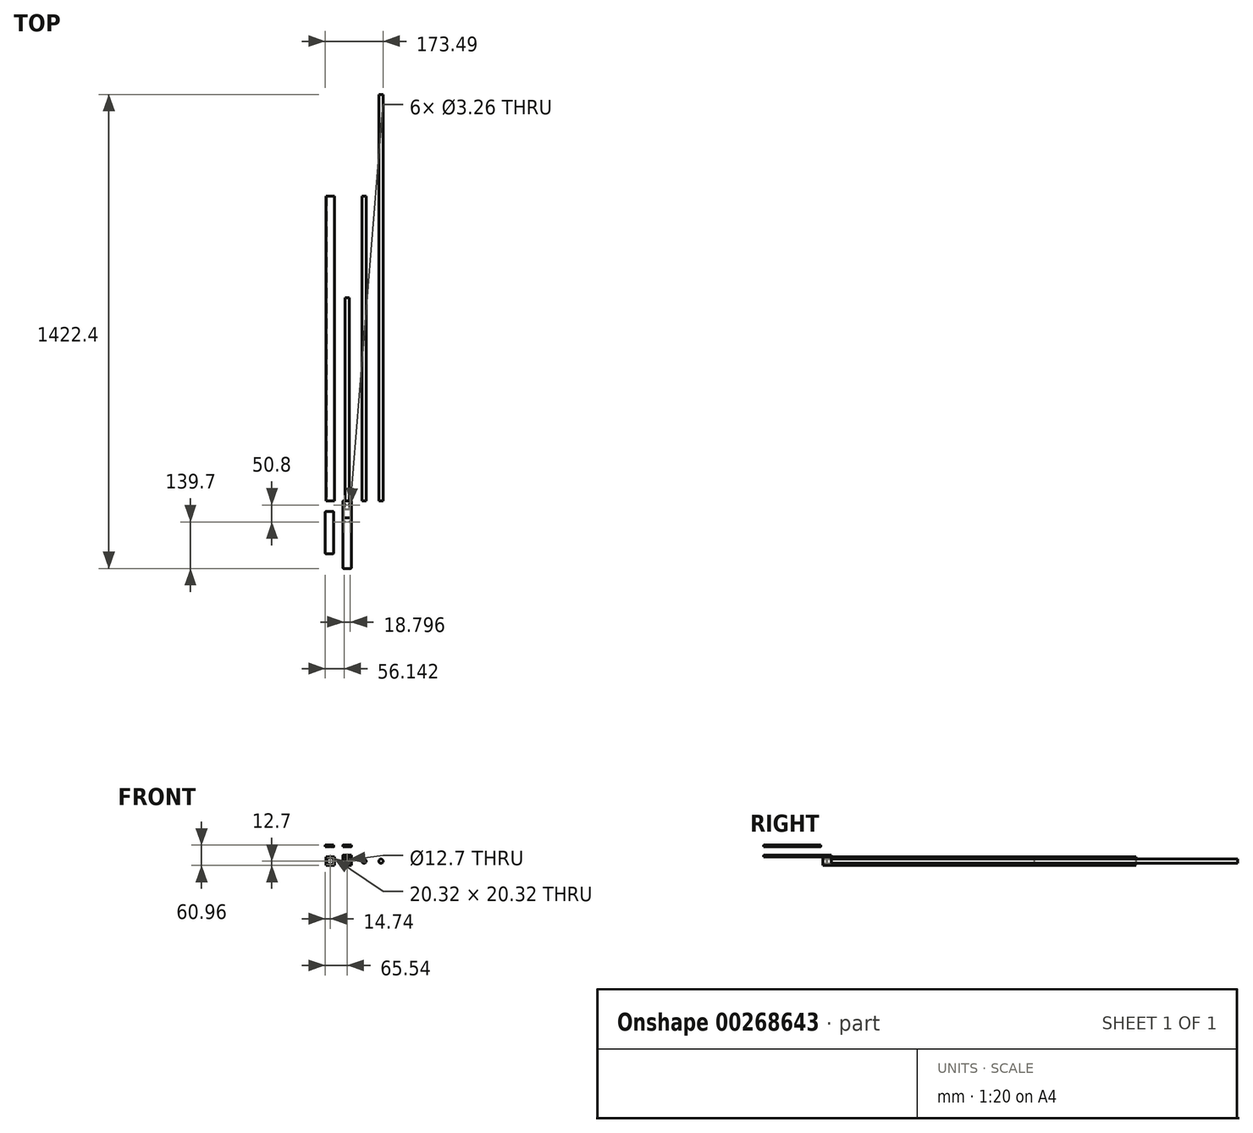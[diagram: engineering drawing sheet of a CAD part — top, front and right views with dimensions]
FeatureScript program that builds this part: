
annotation { "Feature Type Name" : "Feature", "Feature Type Description" : "" }
export const myFeature = defineFeature(function(context is Context, id is Id, definition is map)
    precondition{}
    {
        {
            var Q0;
            Q0=qCreatedBy(makeId("Front.planeOp"),FACE);
            var sketch = newSketch(context, id + "F0", { "sketchPlane" : qUnion([Q0])});
            skCircle(sketch, "E0", {"center": v(0, 0) * mm, "radius": 6.35 * mm});
            skCircle(sketch, "E1", {"center": v(-50.8, 0) * mm, "radius": 6.35 * mm});
            skCircle(sketch, "E2", {"center": v(50.8, 0) * mm, "radius": 6.35 * mm});
            skSolve(sketch);
        }
        {
            var Q0;
            Q0=makeQuery(id+"F0.imprint","IMPRINT",FACE,{"disambiguationData":[TD([[makeQuery(id+"F0.imprint","IMPRINT",EDGE,{"derivedFrom":sQuery(id+"F0.wireOp",EDGE,"E1")}),1.0]])]});
            extrude(context, id + "F1", {"entities" : qUnion([Q0]), "oppositeDirection" : true, "depth" : 609.6 * mm});
        }
        {
            var Q0;
            Q0=makeQuery(id+"F0.imprint","IMPRINT",FACE,{"disambiguationData":[TD([[makeQuery(id+"F0.imprint","IMPRINT",EDGE,{"derivedFrom":sQuery(id+"F0.wireOp",EDGE,"E0")}),1.0]])]});
            var Q1;
            Q1=sQuery(id+"F0.wireOp",EDGE,"E0");
            extrude(context, id + "F2", {"entities" : qUnion([Q0]), "surfaceEntities" : qUnion([Q1]), "oppositeDirection" : true, "depth" : 914.4 * mm});
        }
        {
            var Q0;
            Q0=makeQuery(id+"F0.imprint","IMPRINT",FACE,{"disambiguationData":[TD([[makeQuery(id+"F0.imprint","IMPRINT",EDGE,{"derivedFrom":sQuery(id+"F0.wireOp",EDGE,"E2")}),1.0]])]});
            extrude(context, id + "F3", {"entities" : qUnion([Q0]), "oppositeDirection" : true, "depth" : 1219.2 * mm});
        }
        {
            var Q0;
            Q0=makeQuery(id+"F0.imprint","IMPRINT",FACE,{"disambiguationData":[TD([[makeQuery(id+"F0.imprint","IMPRINT",EDGE,{"derivedFrom":sQuery(id+"F0.wireOp",EDGE,"E1")}),1.0]])]});
            var sketch = newSketch(context, id + "F4", { "sketchPlane" : qUnion([Q0])});
            skCircle(sketch, "E3.0", {"center": v(-50.8, 0) * mm, "radius": 6.35 * mm});
            skLineSegment(sketch, "E4.bottom", {"start": v(-63.5, 12.7) * mm, "end": v(-38.1, 12.7) * mm});
            skLineSegment(sketch, "E4.top", {"start": v(-63.5, -12.7) * mm, "end": v(-38.1, -12.7) * mm});
            skLineSegment(sketch, "E4.left", {"start": v(-63.5, 12.7) * mm, "end": v(-63.5, -12.7) * mm});
            skLineSegment(sketch, "E4.right", {"start": v(-38.1, 12.7) * mm, "end": v(-38.1, -12.7) * mm});
            skSolve(sketch);
        }
        {
            var Q0;
            Q0=makeQuery(id+"F4.imprint","IMPRINT",FACE,{"disambiguationData":[TD([[makeQuery(id+"F4.imprint","IMPRINT",EDGE,{"derivedFrom":sQuery(id+"F4.wireOp",EDGE,"E3.0")}),-1.0]])]});
            extrude(context, id + "F5", {"entities" : qUnion([Q0]), "depth" : 25.4 * mm});
        }
        {
            var Q0;
            Q0=makeQuery(id+"F5.opExtrude","SWEPT_FACE",FACE,{"disambiguationData":[OSD([sQuery(id+"F4.wireOp",EDGE,"E4.bottom")])]});
            var sketch = newSketch(context, id + "F6", { "sketchPlane" : qUnion([Q0])});
            skLineSegment(sketch, "E5", {"start": v(-60.2, 0) * mm, "end": v(-60.2, -25.4) * mm, "construction": true});
            skLineSegment(sketch, "E6", {"start": v(-50.8, 0) * mm, "end": v(-50.8, -25.4) * mm, "construction": true});
            skPoint(sketch, "E7", {"position": v(-60.2, -12.7) * mm});
            skPoint(sketch, "E8.MirrorP", {"position": v(-41.4, -12.7) * mm});
            skSolve(sketch);
        }
        {
            var Q0;
            Q0=sQuery(id+"F6.wireOp",VERTEX,"E7");
            var Q1;
            Q1=sQuery(id+"F6.wireOp",VERTEX,"E8.MirrorP");
            var Q2;
            Q2=makeQuery(id+"F5.opExtrude","SWEPT_BODY",BODY,{"disambiguationData":[OSD([sQuery(id+"F4.wireOp",EDGE,"E3.0"),sQuery(id+"F4.wireOp",EDGE,"E4.bottom"),sQuery(id+"F4.wireOp",EDGE,"E4.top"),sQuery(id+"F4.wireOp",EDGE,"E4.left"),sQuery(id+"F4.wireOp",EDGE,"E4.right")])]});
            hole(context, id + "F7", {"style" : HoleStyle.C_SINK, "endStyle" : HoleEndStyle.BLIND, "standardTappedOrClearance" : lookupTablePath({ "standard" : "ANSI", "fit" : "Normal (ASME)", "size" : "#4", "type" : "Clearance" }), "standardBlindInLast" : lookupTablePath({ "fit" : "Free", "standard" : "ANSI", "size" : "#4", "type" : "Clearance" }), "holeDiameter" : 3.26 * mm, "cSinkDiameter" : 6.48 * mm, "cSinkAngle" : 82 * degree, "holeDepth" : 25.4 * mm, "tappedDepth" : 12.7 * mm, "tapClearance" : 3, "startFromSketch" : true, "locations" : qUnion([Q0, Q1]), "scope" : qUnion([Q2])});
        }
        {
            var Q0;
            Q0=makeQuery(id+"F5.opExtrude","SWEPT_FACE",FACE,{"disambiguationData":[OSD([sQuery(id+"F4.wireOp",EDGE,"E4.bottom")])]});
            var sketch = newSketch(context, id + "F8", { "sketchPlane" : qUnion([Q0])});
            skCircle(sketch, "E9.0", {"center": v(-60.2, -12.7) * mm, "radius": 1.63 * mm});
            skCircle(sketch, "E10.0", {"center": v(-41.4, -12.7) * mm, "radius": 1.63 * mm});
            skLineSegment(sketch, "E11.bottom", {"start": v(-38.1, 0) * mm, "end": v(-63.5, 0) * mm});
            skLineSegment(sketch, "E11.top", {"start": v(-38.1, -203.2) * mm, "end": v(-63.5, -203.2) * mm});
            skLineSegment(sketch, "E11.left", {"start": v(-38.1, 0) * mm, "end": v(-38.1, -203.2) * mm});
            skLineSegment(sketch, "E11.right", {"start": v(-63.5, 0) * mm, "end": v(-63.5, -203.2) * mm});
            skLineSegment(sketch, "E12", {"start": v(-63.5, -101.6) * mm, "end": v(-38.1, -101.6) * mm, "construction": true});
            skCircle(sketch, "E13.0", {"center": v(-60.2, -12.7) * mm, "radius": 3.24 * mm});
            skCircle(sketch, "E14.0", {"center": v(-41.4, -12.7) * mm, "radius": 3.24 * mm});
            skSolve(sketch);
        }
        {
            var Q0;
            {var subQ0=sQuery(id+"F8.wireOp",EDGE,"E11.top");Q0=makeQuery(id+"F8.imprint","IMPRINT",FACE,{"disambiguationData":[TD([[makeQuery(id+"F8.imprint","IMPRINT",EDGE,{"derivedFrom":subQ0}),-1.0]])]});}
            var Q1;
            Q1=makeQuery(id+"F8.imprint","IMPRINT",FACE,{"disambiguationData":[TD([[makeQuery(id+"F8.imprint","IMPRINT",EDGE,{"derivedFrom":sQuery(id+"F8.wireOp",EDGE,"E9.0")}),-1.0]])]});
            var Q2;
            Q2=makeQuery(id+"F8.imprint","IMPRINT",FACE,{"disambiguationData":[TD([[makeQuery(id+"F8.imprint","IMPRINT",EDGE,{"derivedFrom":sQuery(id+"F8.wireOp",EDGE,"E10.0")}),-1.0]])]});
            var Q3;
            {var subQ1=sQuery(id+"F8.wireOp",EDGE,"E11.bottom");Q3=makeQuery(id+"F8.imprint","IMPRINT",FACE,{"disambiguationData":[TD([[makeQuery(id+"F8.imprint","IMPRINT",EDGE,{"derivedFrom":subQ1}),-1.0]])]});}
            var Q4;
            Q4=makeQuery(id+"F8.imprint","IMPRINT",FACE,{"disambiguationData":[TD([[makeQuery(id+"F8.imprint","IMPRINT",EDGE,{"derivedFrom":sQuery(id+"F8.wireOp",EDGE,"E9.0")}),1.0]])]});
            var Q5;
            Q5=makeQuery(id+"F8.imprint","IMPRINT",FACE,{"disambiguationData":[TD([[makeQuery(id+"F8.imprint","IMPRINT",EDGE,{"derivedFrom":sQuery(id+"F8.wireOp",EDGE,"E10.0")}),1.0]])]});
            extrude(context, id + "F9", {"entities" : qUnion([Q0, Q1, Q2, Q3, Q4, Q5]), "depth" : 5.08 * mm});
        }
        {
            var Q0;
            Q0=makeQuery(id+"F9.opExtrude","SWEPT_EDGE",EDGE,{"disambiguationData":[OSD([sQuery(id+"F8.wireOp",EDGE,"E11.bottom"),sQuery(id+"F8.wireOp",EDGE,"E11.left")])]});
            var Q1;
            Q1=makeQuery(id+"F9.opExtrude","SWEPT_EDGE",EDGE,{"disambiguationData":[OSD([sQuery(id+"F8.wireOp",EDGE,"E11.bottom"),sQuery(id+"F8.wireOp",EDGE,"E11.right")])]});
            var Q2;
            Q2=makeQuery(id+"F9.opExtrude","SWEPT_EDGE",EDGE,{"disambiguationData":[OSD([sQuery(id+"F8.wireOp",EDGE,"E11.top"),sQuery(id+"F8.wireOp",EDGE,"E11.left")])]});
            var Q3;
            Q3=makeQuery(id+"F9.opExtrude","SWEPT_EDGE",EDGE,{"disambiguationData":[OSD([sQuery(id+"F8.wireOp",EDGE,"E11.top"),sQuery(id+"F8.wireOp",EDGE,"E11.right")])]});
            fillet(context, id + "F10", {"entities" : qUnion([Q0, Q1, Q2, Q3]), "radius" : 2.54 * mm, "tangentPropagation" : true, "allowEdgeOverflow" : false});
        }
        {
            var Q0;
            Q0=makeQuery(id+"F9.opExtrude","CAP_FACE",FACE,{"disambiguationData":[OSD([sQuery(id+"F8.wireOp",EDGE,"E11.bottom"),sQuery(id+"F8.wireOp",EDGE,"E11.top"),sQuery(id+"F8.wireOp",EDGE,"E11.left"),sQuery(id+"F8.wireOp",EDGE,"E11.right")])],"isStart":false});
            var sketch = newSketch(context, id + "F11", { "sketchPlane" : qUnion([Q0])});
            skCircle(sketch, "E15.0", {"center": v(-41.4, -12.7) * mm, "radius": 1.63 * mm});
            skCircle(sketch, "E16.0", {"center": v(-60.2, -12.7) * mm, "radius": 1.63 * mm});
            skSolve(sketch);
        }
        {
            var Q0;
            Q0=sQuery(id+"F11.wireOp",VERTEX,"E16.0.center");
            var Q1;
            Q1=sQuery(id+"F11.wireOp",VERTEX,"E15.0.center");
            var Q2;
            Q2=makeQuery(id+"F9.opExtrude","SWEPT_BODY",BODY,{"disambiguationData":[OSD([sQuery(id+"F8.wireOp",EDGE,"E11.bottom"),sQuery(id+"F8.wireOp",EDGE,"E11.top"),sQuery(id+"F8.wireOp",EDGE,"E11.left"),sQuery(id+"F8.wireOp",EDGE,"E11.right")])]});
            hole(context, id + "F12", {"style" : HoleStyle.C_SINK, "endStyle" : HoleEndStyle.BLIND, "standardTappedOrClearance" : lookupTablePath({ "standard" : "ANSI", "fit" : "Normal (ASME)", "size" : "#4", "type" : "Clearance" }), "standardBlindInLast" : lookupTablePath({ "fit" : "Free", "standard" : "ANSI", "size" : "#4", "type" : "Clearance" }), "holeDiameter" : 3.26 * mm, "cSinkDiameter" : 6.48 * mm, "cSinkAngle" : 82 * degree, "holeDepth" : 25.4 * mm, "tappedDepth" : 12.7 * mm, "tapClearance" : 3, "startFromSketch" : true, "locations" : qUnion([Q0, Q1]), "scope" : qUnion([Q2])});
        }
        {
            var Q0;
            Q0=makeQuery(id+"F9.opExtrude","CAP_EDGE",EDGE,{"disambiguationData":[OSD([sQuery(id+"F8.wireOp",EDGE,"E11.right")])],"isStart":false});
            cPoint(context, id + "F13", {"entities" : qUnion([Q0]), "parameter" : 0.5});
        }
        {
            var Q0;
            Q0=qCreatedBy(makeId("Front.planeOp"),FACE);
            var Q1;
            Q1 = qCreatedBy(id + "F13" ,VERTEX);
            cPlane(context, id + "F14", {"entities" : qUnion([Q0, Q1]), "cplaneType" : CPlaneType.PLANE_POINT, "offset" : 25.4 * mm, "width" : 152.4 * mm, "height" : 152.4 * mm});
        }
        {
            var Q0;
            Q0=makeQuery(id+"F9.opExtrude","CAP_FACE",FACE,{"disambiguationData":[OSD([sQuery(id+"F8.wireOp",EDGE,"E11.bottom"),sQuery(id+"F8.wireOp",EDGE,"E11.top"),sQuery(id+"F8.wireOp",EDGE,"E11.left"),sQuery(id+"F8.wireOp",EDGE,"E11.right")])],"isStart":false});
            cPlane(context, id + "F15", {"entities" : qUnion([Q0]), "cplaneType" : CPlaneType.OFFSET, "offset" : 25.4 * mm, "width" : 152.4 * mm, "height" : 152.4 * mm});
        }
        {
            var Q0;
            Q0=qCreatedBy(id+"F15.planeOp",FACE);
            var sketch = newSketch(context, id + "F16", { "sketchPlane" : qUnion([Q0])});
            skLineSegment(sketch, "E17.0.0", {"start": v(-63.5, -2.54) * mm, "end": v(-63.5, -200.66) * mm});
            skArc(sketch, "E17.0.1", {"start": v(-63.5, -200.66) * mm, "mid": v(-62.76, -202.46) * mm, "end": v(-60.96, -203.2) * mm});
            skLineSegment(sketch, "E17.0.2", {"start": v(-60.96, -203.2) * mm, "end": v(-40.64, -203.2) * mm});
            skArc(sketch, "E17.0.3", {"start": v(-40.64, -203.2) * mm, "mid": v(-38.84, -202.46) * mm, "end": v(-38.1, -200.66) * mm});
            skLineSegment(sketch, "E17.0.4", {"start": v(-38.1, -200.66) * mm, "end": v(-38.1, -2.54) * mm});
            skArc(sketch, "E17.0.5", {"start": v(-38.1, -2.54) * mm, "mid": v(-38.84, -0.74) * mm, "end": v(-40.64, 0) * mm});
            skLineSegment(sketch, "E17.0.6", {"start": v(-40.64, 0) * mm, "end": v(-60.96, 0) * mm});
            skArc(sketch, "E17.0.7", {"start": v(-60.96, 0) * mm, "mid": v(-62.76, -0.74) * mm, "end": v(-63.5, -2.54) * mm});
            skLineSegment(sketch, "E18", {"start": v(-63.5, -127) * mm, "end": v(-38.1, -127) * mm, "construction": true});
            skLineSegment(sketch, "E19.MirrorCS", {"start": v(-60.96, -50.8) * mm, "end": v(-40.64, -50.8) * mm});
            skArc(sketch, "E20.MirrorCS", {"start": v(-63.5, -53.34) * mm, "mid": v(-62.76, -51.54) * mm, "end": v(-60.96, -50.8) * mm});
            skArc(sketch, "E21.MirrorCS", {"start": v(-40.64, -50.8) * mm, "mid": v(-38.84, -51.54) * mm, "end": v(-38.1, -53.34) * mm});
            skCircle(sketch, "E22.0", {"center": v(-41.4, -190.5) * mm, "radius": 1.63 * mm});
            skCircle(sketch, "E23.0", {"center": v(-60.2, -190.5) * mm, "radius": 1.63 * mm});
            skCircle(sketch, "E24.MirrorC", {"center": v(-60.2, -63.5) * mm, "radius": 1.63 * mm});
            skCircle(sketch, "E25.MirrorC", {"center": v(-41.4, -63.5) * mm, "radius": 1.63 * mm});
            skSolve(sketch);
        }
        {
            var Q0;
            {var subQ3=sQuery(id+"F16.wireOp",EDGE,"E17.0.1");Q0=makeQuery(id+"F16.imprint","IMPRINT",FACE,{"disambiguationData":[TD([[makeQuery(id+"F16.imprint","IMPRINT",EDGE,{"derivedFrom":subQ3}),1.0]])]});}
            var Q1;
            Q1=makeQuery(id+"F16.imprint","IMPRINT",FACE,{"disambiguationData":[TD([[makeQuery(id+"F16.imprint","IMPRINT",EDGE,{"derivedFrom":sQuery(id+"F16.wireOp",EDGE,"E23.0")}),1.0]])]});
            var Q2;
            Q2=makeQuery(id+"F16.imprint","IMPRINT",FACE,{"disambiguationData":[TD([[makeQuery(id+"F16.imprint","IMPRINT",EDGE,{"derivedFrom":sQuery(id+"F16.wireOp",EDGE,"E22.0")}),1.0]])]});
            var Q3;
            Q3=makeQuery(id+"F16.imprint","IMPRINT",FACE,{"disambiguationData":[TD([[makeQuery(id+"F16.imprint","IMPRINT",EDGE,{"derivedFrom":sQuery(id+"F16.wireOp",EDGE,"E24.MirrorC")}),-1.0]])]});
            var Q4;
            Q4=makeQuery(id+"F16.imprint","IMPRINT",FACE,{"disambiguationData":[TD([[makeQuery(id+"F16.imprint","IMPRINT",EDGE,{"derivedFrom":sQuery(id+"F16.wireOp",EDGE,"E25.MirrorC")}),-1.0]])]});
            extrude(context, id + "F17", {"entities" : qUnion([Q0, Q1, Q2, Q3, Q4]), "depth" : 5.08 * mm});
        }
        {
            var Q0;
            Q0=qCreatedBy(makeId("Front.planeOp"),FACE);
            var sketch = newSketch(context, id + "F18", { "sketchPlane" : qUnion([Q0])});
            skPoint(sketch, "E26", {"position": v(-101.6, 0) * mm});
            skLineSegment(sketch, "E27.bottom", {"start": v(-114.3, 12.7) * mm, "end": v(-88.9, 12.7) * mm});
            skLineSegment(sketch, "E27.top", {"start": v(-114.3, -12.7) * mm, "end": v(-88.9, -12.7) * mm});
            skLineSegment(sketch, "E27.left", {"start": v(-114.3, 12.7) * mm, "end": v(-114.3, -12.7) * mm});
            skLineSegment(sketch, "E27.right", {"start": v(-88.9, 12.7) * mm, "end": v(-88.9, -12.7) * mm});
            skLineSegment(sketch, "E28.bottom", {"start": v(-111.76, 10.16) * mm, "end": v(-91.44, 10.16) * mm});
            skLineSegment(sketch, "E28.top", {"start": v(-111.76, -10.16) * mm, "end": v(-91.44, -10.16) * mm});
            skLineSegment(sketch, "E28.left", {"start": v(-111.76, 10.16) * mm, "end": v(-111.76, -10.16) * mm});
            skLineSegment(sketch, "E28.right", {"start": v(-91.44, 10.16) * mm, "end": v(-91.44, -10.16) * mm});
            skLineSegment(sketch, "E29", {"start": v(-127, 0) * mm, "end": v(-127, 14.96) * mm, "construction": true});
            skLineSegment(sketch, "E30.MirrorCS", {"start": v(-142.24, 10.16) * mm, "end": v(-162.56, 10.16) * mm});
            skPoint(sketch, "E31.MirrorP", {"position": v(-152.4, 0) * mm});
            skLineSegment(sketch, "E32.MirrorCS", {"start": v(-139.7, 12.7) * mm, "end": v(-139.7, -12.7) * mm});
            skLineSegment(sketch, "E33.MirrorCS", {"start": v(-165.1, 12.7) * mm, "end": v(-165.1, -12.7) * mm});
            skLineSegment(sketch, "E34.MirrorCS", {"start": v(-139.7, -12.7) * mm, "end": v(-165.1, -12.7) * mm});
            skLineSegment(sketch, "E35.MirrorCS", {"start": v(-139.7, 12.7) * mm, "end": v(-165.1, 12.7) * mm});
            skLineSegment(sketch, "E36.MirrorCS", {"start": v(-142.24, -10.16) * mm, "end": v(-162.56, -10.16) * mm});
            skLineSegment(sketch, "E37.MirrorCS", {"start": v(-142.24, 10.16) * mm, "end": v(-142.24, -10.16) * mm});
            skLineSegment(sketch, "E38.MirrorCS", {"start": v(-162.56, 10.16) * mm, "end": v(-162.56, -10.16) * mm});
            skSolve(sketch);
        }
        {
            var Q0;
            Q0=makeQuery(id+"F18.imprint","IMPRINT",FACE,{"disambiguationData":[TD([[makeQuery(id+"F18.imprint","IMPRINT",EDGE,{"derivedFrom":sQuery(id+"F18.wireOp",EDGE,"E27.bottom")}),-1.0]])]});
            extrude(context, id + "F19", {"entities" : qUnion([Q0]), "oppositeDirection" : true, "depth" : 914.4 * mm});
        }
        {
            var Q0;
            Q0=qCreatedBy(id+"F15.planeOp",FACE);
            var sketch = newSketch(context, id + "F20", { "sketchPlane" : qUnion([Q0])});
            skLineSegment(sketch, "E39.bottom", {"start": v(-90.94, -32.2) * mm, "end": v(-116.34, -32.2) * mm});
            skLineSegment(sketch, "E39.top", {"start": v(-90.94, -159.2) * mm, "end": v(-116.34, -159.2) * mm});
            skLineSegment(sketch, "E39.left", {"start": v(-90.94, -32.2) * mm, "end": v(-90.94, -159.2) * mm});
            skLineSegment(sketch, "E39.right", {"start": v(-116.34, -32.2) * mm, "end": v(-116.34, -159.2) * mm});
            skSolve(sketch);
        }
        {
            var Q0;
            Q0=makeQuery(id+"F20.imprint","IMPRINT",FACE,{"disambiguationData":[TD([[makeQuery(id+"F20.imprint","IMPRINT",EDGE,{"derivedFrom":sQuery(id+"F20.wireOp",EDGE,"E39.bottom")}),1.0]])]});
            extrude(context, id + "F21", {"entities" : qUnion([Q0]), "depth" : 5.08 * mm});
        }
        {
            var Q0;
            Q0=makeQuery(id+"F21.opExtrude","SWEPT_EDGE",EDGE,{"disambiguationData":[OSD([sQuery(id+"F20.wireOp",EDGE,"E39.bottom"),sQuery(id+"F20.wireOp",EDGE,"E39.right")])]});
            var Q1;
            Q1=makeQuery(id+"F21.opExtrude","SWEPT_EDGE",EDGE,{"disambiguationData":[OSD([sQuery(id+"F20.wireOp",EDGE,"E39.bottom"),sQuery(id+"F20.wireOp",EDGE,"E39.left")])]});
            var Q2;
            Q2=makeQuery(id+"F21.opExtrude","SWEPT_EDGE",EDGE,{"disambiguationData":[OSD([sQuery(id+"F20.wireOp",EDGE,"E39.top"),sQuery(id+"F20.wireOp",EDGE,"E39.right")])]});
            var Q3;
            Q3=makeQuery(id+"F21.opExtrude","SWEPT_EDGE",EDGE,{"disambiguationData":[OSD([sQuery(id+"F20.wireOp",EDGE,"E39.top"),sQuery(id+"F20.wireOp",EDGE,"E39.left")])]});
            fillet(context, id + "F22", {"entities" : qUnion([Q0, Q1, Q2, Q3]), "radius" : 2.54 * mm, "tangentPropagation" : true, "allowEdgeOverflow" : false});
        }
    });
